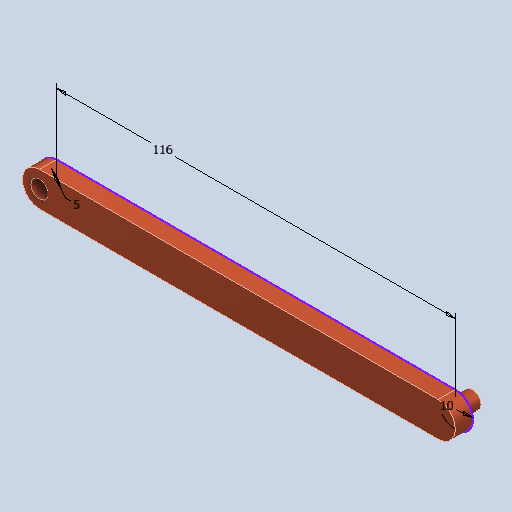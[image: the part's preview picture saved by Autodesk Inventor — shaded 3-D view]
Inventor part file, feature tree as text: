
AUTODESK INVENTOR PART (.ipt)
format: ipt  version: 2022 (Build 260153000, 153)  size: 106,496 bytes
history: native  units: mm
features: extrude x2, sketch x1
ambient origin geometry x8: Origin, YZ Plane, XZ Plane, XY Plane, X Axis, Y Axis, Z Axis, Center Point
bodies: Solid1 (feature_tree)
feature tree (3):
  sketch  "Sketch1"  dims[d0=10.0mm d1=5.0mm d2=116.0mm d3=5.0mm d4=0.0mm d5=5.0mm d6=0.0mm]
  extrude  "Extrusion1"  Depth=5.0mm
  extrude  "Extrusion2"  Depth=5.0mm
